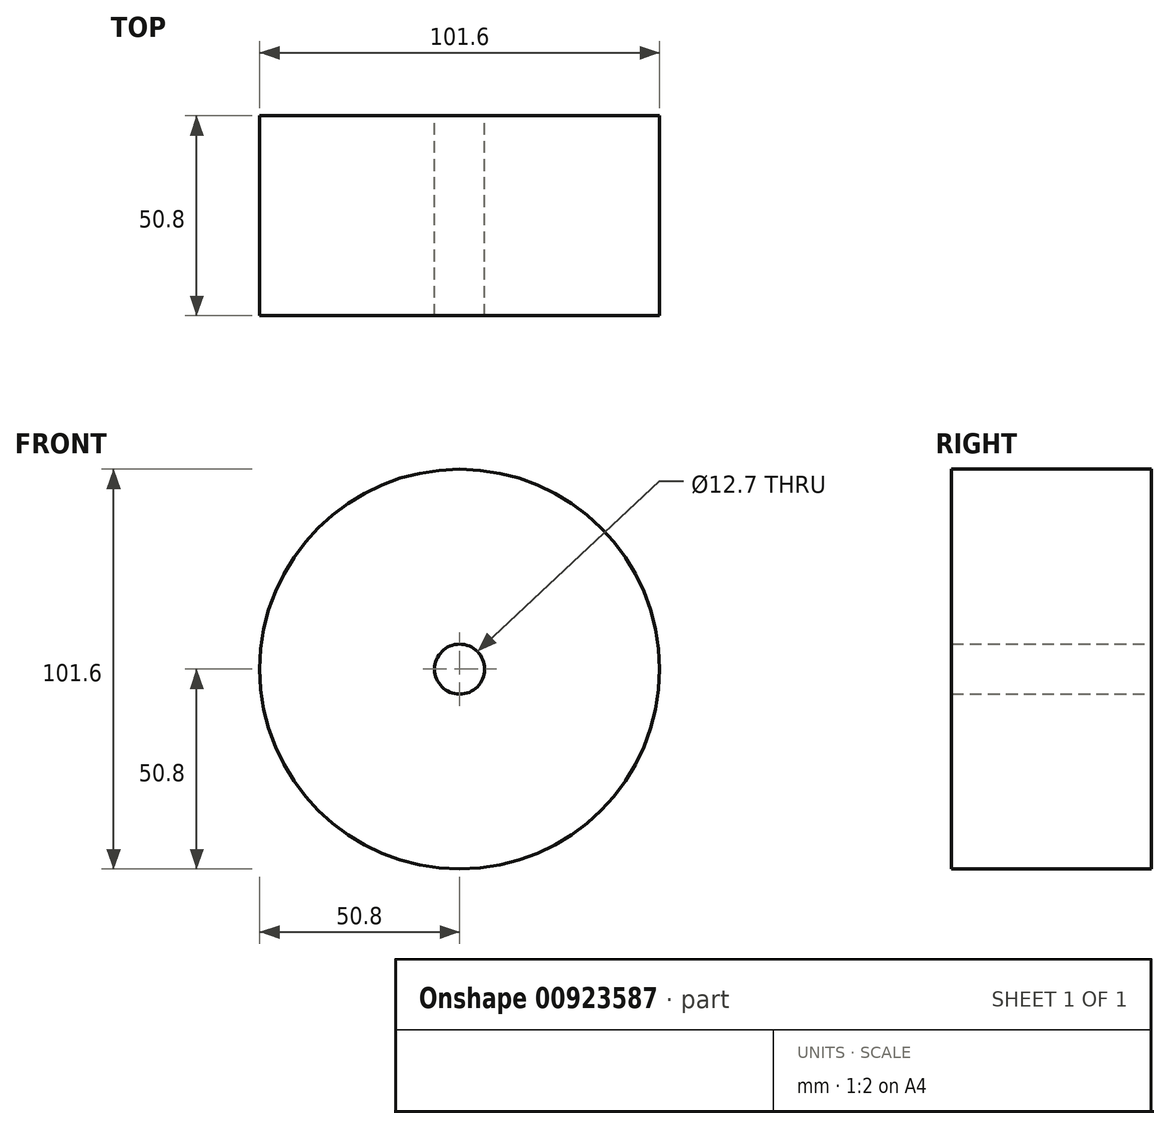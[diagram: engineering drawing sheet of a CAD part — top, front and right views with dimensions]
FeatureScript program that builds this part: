
annotation { "Feature Type Name" : "Feature", "Feature Type Description" : "" }
export const myFeature = defineFeature(function(context is Context, id is Id, definition is map)
    precondition{}
    {
        {
            var Q0;
            Q0=qCreatedBy(makeId("Front.planeOp"),FACE);
            var sketch = newSketch(context, id + "F0", { "sketchPlane" : qUnion([Q0])});
            skCircle(sketch, "E0", {"center": v(0, 0) * mm, "radius": 50.8 * mm});
            skCircle(sketch, "E1", {"center": v(0, 0) * mm, "radius": 6.35 * mm});
            skSolve(sketch);
        }
        {
            var Q0;
            Q0=makeQuery(id+"F0.imprint","IMPRINT",FACE,{"disambiguationData":[TD([[makeQuery(id+"F0.imprint","IMPRINT",EDGE,{"derivedFrom":sQuery(id+"F0.wireOp",EDGE,"E0")}),1.0]])]});
            extrude(context, id + "F1", {"entities" : qUnion([Q0]), "depth" : 50.8 * mm, "offsetDistance" : 25.4 * mm});
        }
    });
